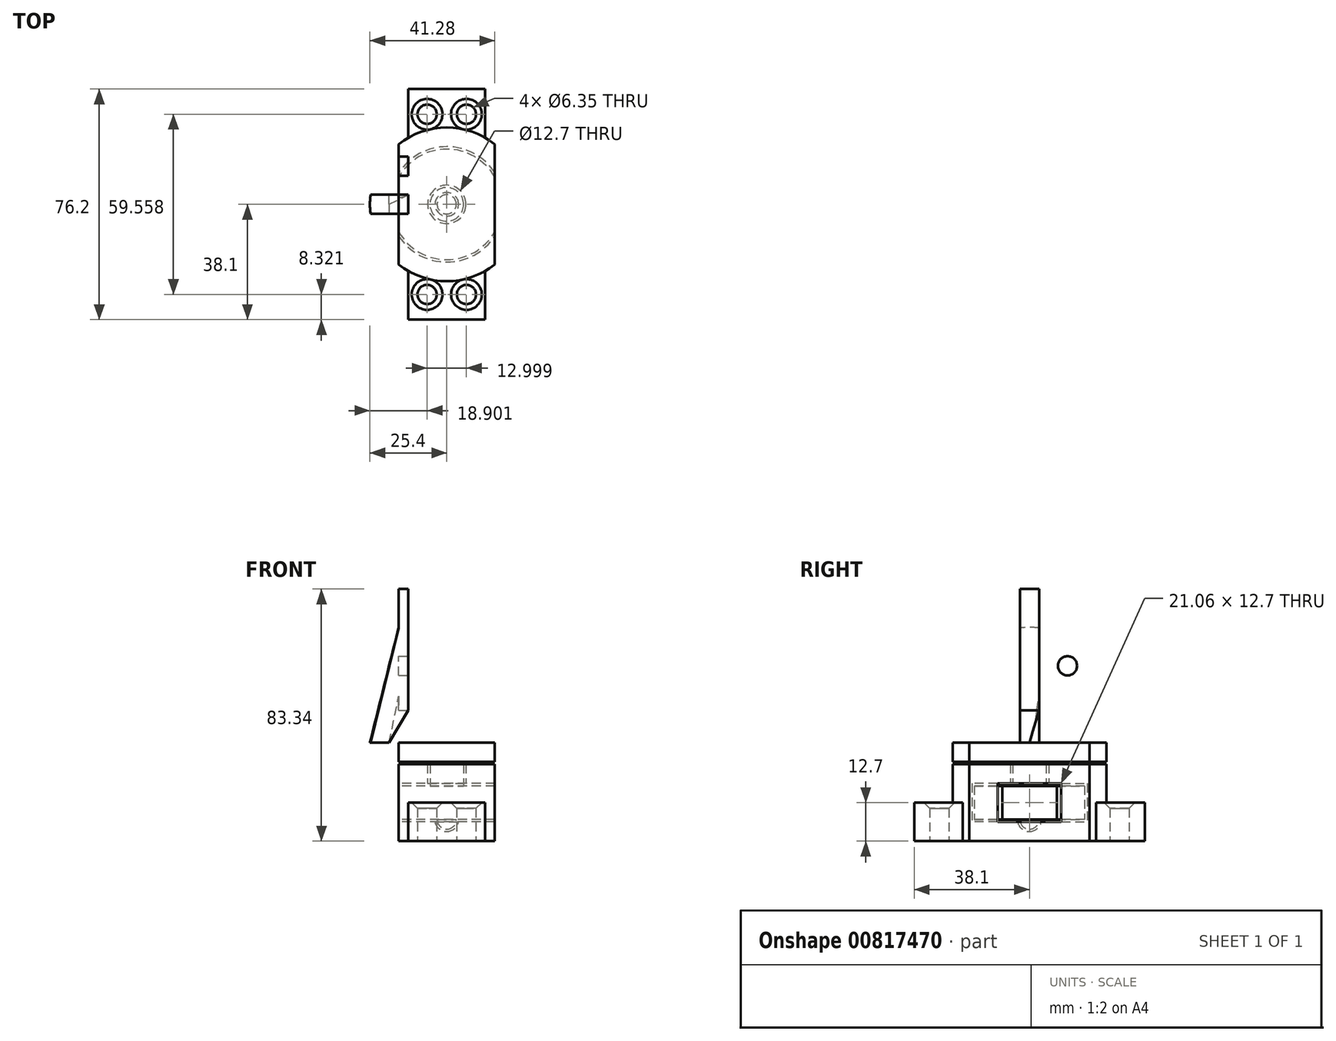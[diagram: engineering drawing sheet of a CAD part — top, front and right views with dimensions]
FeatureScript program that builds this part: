
annotation { "Feature Type Name" : "Feature", "Feature Type Description" : "" }
export const myFeature = defineFeature(function(context is Context, id is Id, definition is map)
    precondition{}
    {
        {
            var Q0;
            Q0=qCreatedBy(makeId("Front.planeOp"),FACE);
            var sketch = newSketch(context, id + "F0", { "sketchPlane" : qUnion([Q0])});
            skLineSegment(sketch, "E0.bottom", {"start": v(0, 0) * mm, "end": v(25.4, 0) * mm});
            skLineSegment(sketch, "E0.top", {"start": v(0, 25.4) * mm, "end": v(19.05, 25.4) * mm});
            skLineSegment(sketch, "E0.left", {"start": v(0, 0) * mm, "end": v(0, 25.4) * mm});
            skLineSegment(sketch, "E0.right", {"start": v(25.4, 0) * mm, "end": v(25.4, 32.54) * mm});
            skLineSegment(sketch, "E1.0", {"start": v(12.7, 6.35) * mm, "end": v(21.51, 6.35) * mm});
            skLineSegment(sketch, "E1.2", {"start": v(6.35, 19.05) * mm, "end": v(19.05, 19.05) * mm});
            skLineSegment(sketch, "E2.0", {"start": v(19.05, 19.05) * mm, "end": v(19.05, 25.4) * mm});
            skLineSegment(sketch, "E3.0", {"start": v(7.14, 7.14) * mm, "end": v(22.23, 7.14) * mm});
            skLineSegment(sketch, "E4.0", {"start": v(12.7, 18.26) * mm, "end": v(19.84, 18.26) * mm});
            skLineSegment(sketch, "E5.0", {"start": v(19.84, 18.26) * mm, "end": v(19.84, 26.2) * mm});
            skLineSegment(sketch, "E6.0", {"start": v(0, 26.2) * mm, "end": v(19.84, 26.2) * mm});
            skLineSegment(sketch, "E7.0", {"start": v(0, 32.54) * mm, "end": v(25.4, 32.54) * mm});
            skLineSegment(sketch, "E8", {"start": v(0, 32.54) * mm, "end": v(0, 26.2) * mm});
            skPoint(sketch, "E9.orphan", {"position": v(6.35, 19.05) * mm});
            skArc(sketch, "E10", {"start": v(22.23, 7.14) * mm, "mid": v(23.15, 4.9) * mm, "end": v(25.4, 3.97) * mm});
            skArc(sketch, "E11.0", {"start": v(21.51, 6.35) * mm, "mid": v(22.89, 4.07) * mm, "end": v(25.4, 3.17) * mm});
            skLineSegment(sketch, "E12", {"start": v(6.35, 19.05) * mm, "end": v(6.35, 6.35) * mm});
            skLineSegment(sketch, "E13", {"start": v(6.35, 6.35) * mm, "end": v(12.7, 6.35) * mm});
            skLineSegment(sketch, "E14", {"start": v(12.7, 18.26) * mm, "end": v(7.14, 18.26) * mm});
            skPoint(sketch, "E14.endSnap0", {"position": v(7.14, 12.7) * mm});
            skLineSegment(sketch, "E15", {"start": v(7.14, 18.26) * mm, "end": v(7.14, 7.14) * mm});
            skPoint(sketch, "E16.orphan", {"position": v(12.7, 7.14) * mm});
            skPoint(sketch, "E17.center.orphan", {"position": v(12.7, 12.7) * mm});
            skPoint(sketch, "E17.start.orphan", {"position": v(12.7, 19.05) * mm});
            skSolve(sketch);
        }
        {
            var Q0;
            Q0 = qSketchRegion(id + "F0", true);
            var Q1;
            Q1=sQuery(id+"F0.wireOp",EDGE,"E0.right");
            revolve(context, id + "F1", {"surfaceOperationType" : NewSurfaceOperationType.NEW, "entities" : qUnion([Q0]), "axis" : qUnion([Q1]), "revolveType" : RevolveType.FULL});
        }
        {
            var Q0;
            Q0=makeQuery(id+"F1.opRevolve","SWEPT_FACE",FACE,{"disambiguationData":[OSD([sQuery(id+"F0.wireOp",EDGE,"E0.bottom")])]});
            var sketch = newSketch(context, id + "F2", { "sketchPlane" : qUnion([Q0])});
            skLineSegment(sketch, "E18", {"start": v(12.7, 38.1) * mm, "end": v(38.1, 38.1) * mm});
            skPoint(sketch, "E19.orphan", {"position": v(50.8, 28.58) * mm});
            skLineSegment(sketch, "E20.MirrorCS", {"start": v(12.7, -38.1) * mm, "end": v(38.1, -38.1) * mm});
            skLineSegment(sketch, "E21.0", {"start": v(12.7, 0) * mm, "end": v(12.7, -38.1) * mm});
            skLineSegment(sketch, "E22.MirrorCS", {"start": v(12.7, 0) * mm, "end": v(12.7, 38.1) * mm});
            skLineSegment(sketch, "E23.MirrorCS", {"start": v(38.1, 0) * mm, "end": v(38.1, -38.1) * mm});
            skLineSegment(sketch, "E24.MirrorCS", {"start": v(38.1, 0) * mm, "end": v(38.1, 38.1) * mm});
            skArc(sketch, "E25.trimOffspring", {"start": v(9.53, 19.83) * mm, "mid": v(0, 0) * mm, "end": v(9.53, -19.83) * mm});
            skCircle(sketch, "E26", {"center": v(18.9, 29.78) * mm, "radius": 3.18 * mm});
            skCircle(sketch, "E27.MirrorC", {"center": v(31.9, 29.78) * mm, "radius": 3.18 * mm});
            skCircle(sketch, "E28.MirrorC", {"center": v(18.9, -29.78) * mm, "radius": 3.18 * mm});
            skCircle(sketch, "E29.MirrorC", {"center": v(31.9, -29.78) * mm, "radius": 3.18 * mm});
            skPoint(sketch, "E30.orphan", {"position": v(0, 38.1) * mm});
            skPoint(sketch, "E31.orphan", {"position": v(50.8, 38.1) * mm});
            skLineSegment(sketch, "E32", {"start": v(25.4, 0) * mm, "end": v(25.4, 10.42) * mm});
            skLineSegment(sketch, "E33", {"start": v(9.53, -19.83) * mm, "end": v(9.53, 19.83) * mm});
            skPoint(sketch, "E34.orphan", {"position": v(9.53, 0) * mm});
            skPoint(sketch, "E35.orphan", {"position": v(6.35, 0) * mm});
            skLineSegment(sketch, "E36.MirrorCS", {"start": v(41.27, -19.83) * mm, "end": v(41.27, 19.83) * mm});
            skArc(sketch, "E37.MirrorCS", {"start": v(41.27, 19.83) * mm, "mid": v(50.8, 0) * mm, "end": v(41.27, -19.83) * mm});
            skPoint(sketch, "E38.orphan", {"position": v(41.27, 19.82) * mm});
            skPoint(sketch, "E39.orphan", {"position": v(9.53, 19.82) * mm});
            skSolve(sketch);
        }
        {
            var Q0;
            Q0=makeQuery(id+"F2.imprint","IMPRINT",FACE,{"disambiguationData":[TD([[makeQuery(id+"F2.imprint","IMPRINT",EDGE,{"derivedFrom":sQuery(id+"F2.wireOp",EDGE,"wc4vmbXe-xo6P-GcEh-rUF0-40qTW4JD2Qwd")}),1.0]])]});
            var Q1;
            Q1=makeQuery(id+"F2.imprint","IMPRINT",FACE,{"disambiguationData":[TD([[makeQuery(id+"F2.imprint","IMPRINT",EDGE,{"derivedFrom":sQuery(id+"F2.wireOp",EDGE,"E25.trimOffspring")}),1.0]])]});
            var Q2;
            {var subQ0=sQuery(id+"F2.wireOp",EDGE,"E37.MirrorCS");Q2=makeQuery(id+"F2.imprint","IMPRINT",FACE,{"disambiguationData":[TD([[makeQuery(id+"F2.imprint","IMPRINT",EDGE,{"derivedFrom":subQ0}),1.0]])]});}
            extrude(context, id + "F3", {"entities" : qUnion([Q0, Q1, Q2]), "operationType" : NewBodyOperationType.REMOVE, "endBound" : BoundingType.THROUGH_ALL, "oppositeDirection" : true, "depth" : 25.4 * mm, "offsetDistance" : 25.4 * mm});
        }
        {
            var Q0;
            {var subQ1=sQuery(id+"F2.wireOp",EDGE,"E20.MirrorCS");Q0=makeQuery(id+"F2.imprint","IMPRINT",FACE,{"disambiguationData":[TD([[makeQuery(id+"F2.imprint","IMPRINT",EDGE,{"derivedFrom":subQ1}),1.0]])]});}
            var Q1;
            {var subQ0=sQuery(id+"F2.wireOp",EDGE,"E18");Q1=makeQuery(id+"F2.imprint","IMPRINT",FACE,{"disambiguationData":[TD([[makeQuery(id+"F2.imprint","IMPRINT",EDGE,{"derivedFrom":subQ0}),-1.0]])]});}
            extrude(context, id + "F4", {"entities" : qUnion([Q0, Q1]), "operationType" : NewBodyOperationType.ADD, "oppositeDirection" : true, "depth" : 12.7 * mm, "offsetDistance" : 25.4 * mm});
        }
        {
            var Q0;
            Q0=makeQuery(id+"F4.opExtrude","CAP_EDGE",EDGE,{"disambiguationData":[OSD([sQuery(id+"F2.wireOp",EDGE,"E29.MirrorC")])],"isStart":false});
            var Q1;
            Q1=makeQuery(id+"F4.opExtrude","CAP_EDGE",EDGE,{"disambiguationData":[OSD([sQuery(id+"F2.wireOp",EDGE,"E28.MirrorC")])],"isStart":false});
            var Q2;
            Q2=makeQuery(id+"F4.opExtrude","CAP_EDGE",EDGE,{"disambiguationData":[OSD([sQuery(id+"F2.wireOp",EDGE,"E26")])],"isStart":false});
            var Q3;
            Q3=makeQuery(id+"F4.opExtrude","CAP_EDGE",EDGE,{"disambiguationData":[OSD([sQuery(id+"F2.wireOp",EDGE,"E27.MirrorC")])],"isStart":false});
            chamfer(context, id + "F5", {"entities" : qUnion([Q0, Q1, Q2, Q3]), "width" : 1.9 * mm, "tangentPropagation" : true});
        }
        {
            var Q0;
            Q0=makeQuery(id+"F1.opRevolve","SWEPT_FACE",FACE,{"disambiguationData":[OSD([sQuery(id+"F0.wireOp",EDGE,"E7.0")])]});
            var sketch = newSketch(context, id + "F6", { "sketchPlane" : qUnion([Q0])});
            skLineSegment(sketch, "E40", {"start": v(12.7, 0) * mm, "end": v(12.7, 22) * mm});
            skLineSegment(sketch, "E41.0", {"start": v(6.35, 0) * mm, "end": v(6.35, 16.8) * mm});
            skLineSegment(sketch, "E42.MirrorCS", {"start": v(6.35, 0) * mm, "end": v(6.35, -16.8) * mm});
            skLineSegment(sketch, "E43.MirrorCS", {"start": v(12.7, 0) * mm, "end": v(12.7, -22) * mm});
            skArc(sketch, "E44", {"start": v(12.7, 22) * mm, "mid": v(9.31, 19.66) * mm, "end": v(6.35, 16.8) * mm});
            skPoint(sketch, "E45.orphan", {"position": v(6.35, 22) * mm});
            skPoint(sketch, "E46.orphan", {"position": v(6.35, -22) * mm});
            skArc(sketch, "E47.trimOffspring", {"start": v(6.35, -16.8) * mm, "mid": v(9.31, -19.66) * mm, "end": v(12.7, -22) * mm});
            skLineSegment(sketch, "E48.0", {"start": v(6.35, 3.18) * mm, "end": v(0.2, 3.18) * mm});
            skLineSegment(sketch, "E49.0", {"start": v(6.35, -3.18) * mm, "end": v(0.2, -3.18) * mm});
            skArc(sketch, "E50.trimOffspring", {"start": v(0.2, 3.18) * mm, "mid": v(0, 0) * mm, "end": v(0.2, -3.17) * mm});
            skSolve(sketch);
        }
        {
            var Q0;
            Q0=makeQuery(id+"F6.imprint","IMPRINT",FACE,{"disambiguationData":[TD([[makeQuery(id+"F6.imprint","IMPRINT",EDGE,{"derivedFrom":sQuery(id+"F6.wireOp",EDGE,"E40")}),1.0]])]});
            extrude(context, id + "F7", {"entities" : qUnion([Q0]), "operationType" : NewBodyOperationType.ADD, "depth" : 50.8 * mm, "offsetDistance" : 25.4 * mm});
        }
        {
            var Q0;
            Q0=makeQuery(id+"F7.opExtrude","SWEPT_FACE",FACE,{"disambiguationData":[OSD([sQuery(id+"F6.wireOp",EDGE,"E40"),sQuery(id+"F6.wireOp",EDGE,"E43.MirrorCS")])]});
            var sketch = newSketch(context, id + "F8", { "sketchPlane" : qUnion([Q0])});
            skLineSegment(sketch, "E51.0", {"start": v(-3.17, 83.34) * mm, "end": v(-3.17, 43.2) * mm});
            skLineSegment(sketch, "E52.0", {"start": v(3.18, 83.34) * mm, "end": v(3.18, 43.2) * mm});
            skCircle(sketch, "E53", {"center": v(-12.59, 57.94) * mm, "radius": 3.18 * mm});
            skCircle(sketch, "E54.MirrorC", {"center": v(12.59, 57.94) * mm, "radius": 3.18 * mm});
            skLineSegment(sketch, "E55", {"start": v(-3.17, 83.34) * mm, "end": v(3.18, 83.34) * mm});
            skLineSegment(sketch, "E56", {"start": v(-3.17, 43.2) * mm, "end": v(3.18, 43.2) * mm});
            skSolve(sketch);
        }
        {
            var Q0;
            Q0=makeQuery(id+"F8.imprint","IMPRINT",FACE,{"disambiguationData":[TD([[makeQuery(id+"F8.imprint","IMPRINT",EDGE,{"derivedFrom":sQuery(id+"F8.wireOp",EDGE,"E53")}),1.0]])]});
            var Q1;
            Q1=makeQuery(id+"F8.imprint","IMPRINT",FACE,{"disambiguationData":[TD([[makeQuery(id+"F8.imprint","IMPRINT",EDGE,{"derivedFrom":sQuery(id+"F8.wireOp",EDGE,"E54.MirrorC")}),-1.0]])]});
            extrude(context, id + "F9", {"entities" : qUnion([Q0, Q1]), "operationType" : NewBodyOperationType.REMOVE, "endBound" : BoundingType.THROUGH_ALL, "oppositeDirection" : true, "depth" : 25.4 * mm, "offsetDistance" : 25.4 * mm});
        }
        {
            var Q1;
            {var subQ4=sQuery(id+"F6.wireOp",EDGE,"E48.0");Q1=makeQuery(id+"F6.imprint","IMPRINT",FACE,{"disambiguationData":[TD([[makeQuery(id+"F6.imprint","IMPRINT",EDGE,{"derivedFrom":subQ4}),1.0]])]});}
            var Q2;
            Q2=makeQuery(id+"F8.imprint","IMPRINT",FACE,{"disambiguationData":[TD([[makeQuery(id+"F8.imprint","IMPRINT",EDGE,{"derivedFrom":sQuery(id+"F8.wireOp",EDGE,"E51.0")}),1.0]])]});
            var Q3;
            Q3=sQuery(id+"F6.wireOp",VERTEX,"E49.0.end");
            var Q4;
            Q4=sQuery(id+"F8.wireOp",VERTEX,"E51.0.start");
            loft(context, id + "F10", {"operationType" : NewBodyOperationType.ADD, "sheetProfilesArray" : [{ "sheetProfileEntities" : qUnion([Q1]) }, { "sheetProfileEntities" : qUnion([Q2]) }], "matchConnections" : true, "connections" : [{ "connectionEntities" : qUnion([Q3, Q4]), "connectionEdgeQueries" : qUnion([]), "connectionEdgeParameters" : [] }]});
        }
    });
